# Revit family: QF_BOURGEAT_Satellite4G_GN6_neutre_1-1_entree325_pleine
name_source: partatom
category: Equipement spécialisé
revit_build: Autodesk Revit 2015 (Build: 20140606_1530(x64)
units: mm (PartAtom-declared; Revit-internal decimal feet)

## types (4) — shared parameters
Certification = NF hygiene alimentaire
Charge max = 60.00 kg
Diametre_roue = 80 mm  [stored 0.262467 ft]
Fabricant = BOURGEAT
Fréquence = 50 Hz
Hauteur hors tout = 690 mm  [stored 2.26378 ft]
Hauteur_porte = 543 mm  [stored 1.7815 ft]
Hauteur_roue = 107 mm  [stored 0.35105 ft]
Indice de protection = IP25
Intensité nominale = 4 A
Largeur_porte = 501 mm
Longueur hors tout = 547 mm
Longueur_poignees_laterales = 665 mm  [stored 2.18176 ft]
Materiau_Poignee_porte = B_Elastomère_TPE_S
Materiau_bac = Acier inoxydable, brossé
Materiau_bandage = B_Elastomère_TPE_S
Materiau_porte = Acier inoxydable, brossé
Materiau_vitre = Verre, vitrage transparent, trempé
Nature isolant = Mousse sans PU
Phase = 2
Pos_V_IHM = 38 mm  [stored 0.124672 ft]
Profondeur hors tout = 821 mm  [stored 2.69357 ft]
Puissance électrique  = 950 W
Spécification du Fabricant = Satellite 4G
Tension = 230 V
URL catalogue = http://www.bourgeat.fr

## per-type parameters (varying)
| type | Consommation énergétique | Hauteur_poignee_porte_sol | Hauteur_poignees_laterales | Humidification | Modèle | Poids net à vide | Poignee_droite | Poignee_gauche |
| GN6_sans_humidification_porte_inox_tirant_gauche | 0.27Kwh/h NFD40-016 | 241 mm  [stored 0.790682 ft] | 804 mm  [stored 2.6378 ft] | Non | 843206 | 50.00 kg | Non | Oui |
| GN6_humidification_porte_inox_tirant_gauche | 0.24Kwh/h NFD40-016 | 280 mm  [stored 0.918635 ft] | 804 mm  [stored 2.6378 ft] | Oui | 843306 | 50.00 kg | Non | Oui |
| GN6_sans_humidification_porte_inox_tirant_droit | 0.24Kwh/h NFD40-016 | 280 mm  [stored 0.918635 ft] | 804 mm  [stored 2.6378 ft] | Non | 843206 + 844000 | 50.00 kg | Oui | Non |
| GN6_humidification_porte_inox_tirant_droit | 0.24Kwh/h NFD40-016 | 280 mm  [stored 0.918635 ft] | 791 mm | Oui | 843306 + 844000 | 60.00 kg | Oui | Non |

note: [stored X ft] marks values corroborated as IEEE doubles in the binary element streams (Revit-internal decimal feet)
